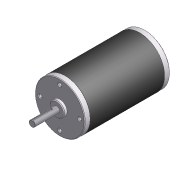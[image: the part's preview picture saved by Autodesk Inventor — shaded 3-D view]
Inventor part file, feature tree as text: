
AUTODESK INVENTOR PART (.ipt)
format: ipt  version: unknown  size: 278,528 bytes
history: native  units: mm (DEFAULTED — no unit token found)
features: sketch x9, extrude x7, chamfer x4, hole x2, pattern_circular x2, fillet x2
ambient origin geometry x8: Origin, YZ Plane, XZ Plane, XY Plane, X Axis, Y Axis, Z Axis, Center Point
bodies: Solid1 (feature_tree)
feature tree (26):
  extrude  "Extrusion1"  Depth=7.0mm TaperAngle=0.0deg
  extrude  "Extrusion2"  Depth=3.9878mm TaperAngle=0.0deg
  chamfer  "Chamfer1"  Distance=1.0mm
  hole  "Hole2"  [1 undecoded]
  pattern_circular  "Circular Pattern2"  Count=4 Angle=90.0deg
  chamfer  "Chamfer3"  Distance=31.623mm
  extrude  "Extrusion3"  Depth=12.7mm
  fillet  "Fillet1"  Radius=2.0mm
  extrude  "Extrusion4"  Depth=25.6286mm TaperAngle=0.0deg
  extrude  "Extrusion5"  Depth=95.6056mm TaperAngle=0.0deg
  extrude  "Extrusion6"  Depth=7.0mm TaperAngle=0.0deg
  extrude  "Extrusion7"  Depth=4.1148mm TaperAngle=0.0deg
  hole  "Hole3"  [1 undecoded]
  chamfer  "Chamfer2"  Distance=0.762mm
  pattern_circular  "Circular Pattern3"  [2 undecoded]
  fillet  "Fillet2"  Radius=20.0mm
  chamfer  "Chamfer4"  Distance=0.25mm
  sketch  "Sketch1"  dims[d0=64.008mm d1=7.0mm d2=0.0mm]
  sketch  "Sketch2"  dims[d3=19.05mm d4=3.9878mm d5=0.0mm d6=1.0mm d7=1.0mm]
  sketch  "Sketch4"  dims[d18=3.9624mm d19=9.525mm d20=6.35mm d21=60.0deg d22=19.05mm d23=20.594885mm d24=25.4mm d25=40.0mm d27=90.0deg]
  sketch  "Sketch5"  dims[d28=7.9502mm d29=31.623mm d30=0.0mm]
  sketch  "Sketch7"  dims[d31=0.79375mm d33=12.7mm d34=2.0mm]
  sketch  "Sketch8"  dims[d35=3.0mm d36=25.6286mm d37=0.0mm]
  sketch  "Sketch9"  dims[d38=64.4144mm d39=95.6056mm d40=0.0mm]
  sketch  "Sketch10"  dims[d41=64.008mm d42=7.0mm d43=0.0mm]
  sketch  "Sketch11"  dims[d44=30.1498mm d45=4.1148mm d46=0.0mm d47=5.08mm d48=12.7mm d49=9.906mm d50=4.572mm d51=14.3117mm d52=7.62mm d53=20.594885mm d54=0.508mm d55=3.175mm d56=0.762mm d57=0.762mm d58=3.175mm d59=20.0mm d61=360.0deg d62=0.25mm d63=3.175mm d64=45.0deg d65=45.0deg d66=45.0deg d67=45.0deg]
note: 4 required parameter values undecoded (feature->parameter linkage not recoverable at this tier; creation-order binding heuristic only, values carry confidence <= 0.55)
